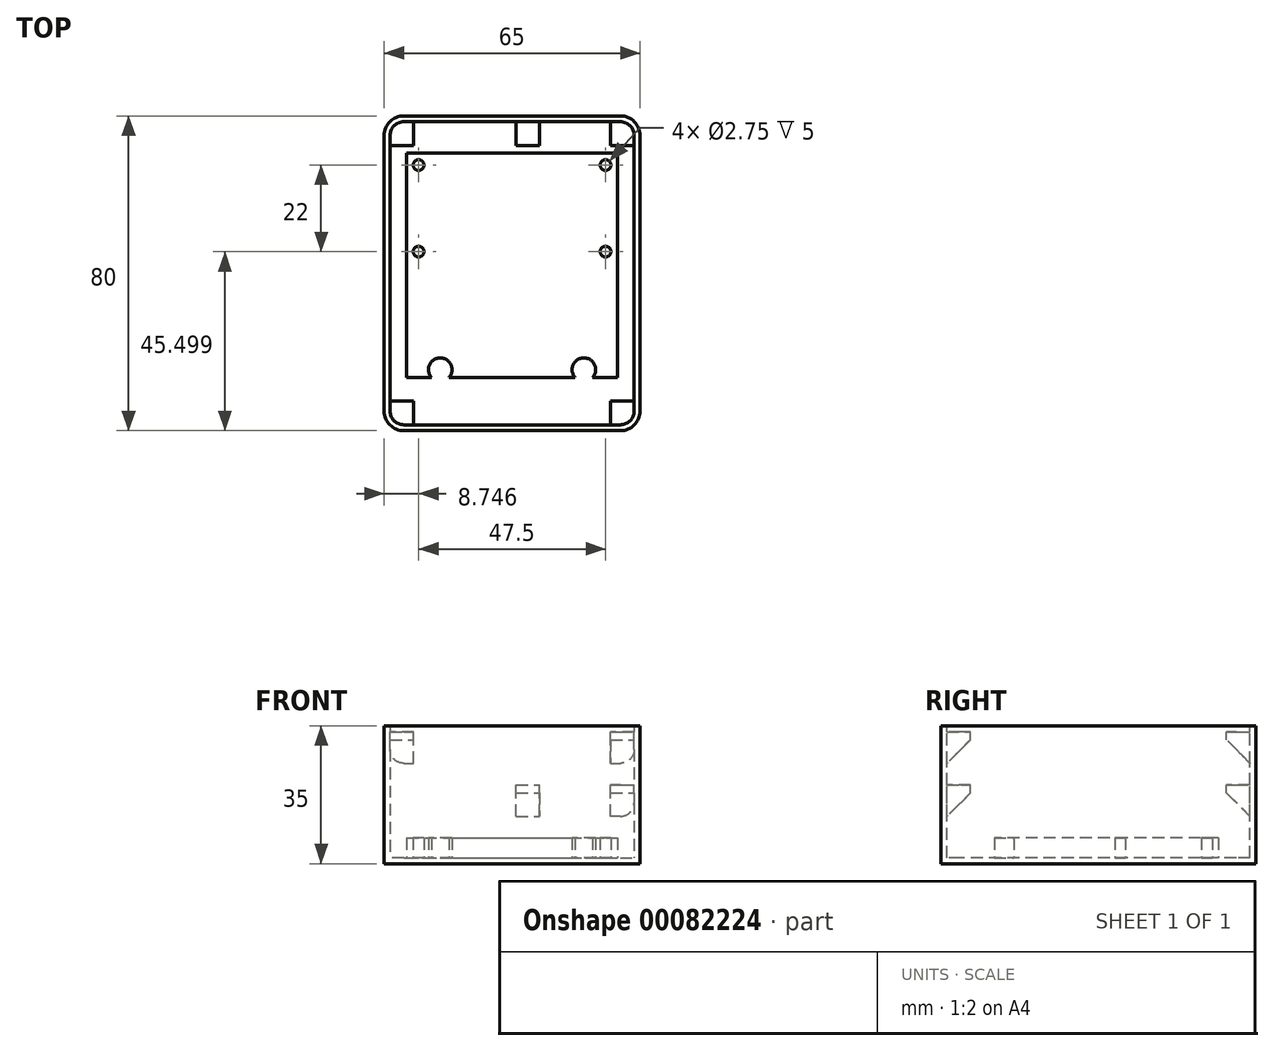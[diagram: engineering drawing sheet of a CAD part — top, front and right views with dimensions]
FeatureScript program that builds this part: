
annotation { "Feature Type Name" : "Feature", "Feature Type Description" : "" }
export const myFeature = defineFeature(function(context is Context, id is Id, definition is map)
    precondition{}
    {
        {
            var Q0;
            Q0=qCreatedBy(makeId("Top.planeOp"),FACE);
            var sketch = newSketch(context, id + "F0", { "sketchPlane" : qUnion([Q0])});
            skLineSegment(sketch, "E0.bottom", {"start": v(-31.3, 26.17) * mm, "end": v(33.7, 26.17) * mm});
            skLineSegment(sketch, "E0.top", {"start": v(-31.3, -53.83) * mm, "end": v(33.7, -53.83) * mm});
            skLineSegment(sketch, "E0.left", {"start": v(-31.3, 26.17) * mm, "end": v(-31.3, -53.83) * mm});
            skLineSegment(sketch, "E0.right", {"start": v(33.7, 26.17) * mm, "end": v(33.7, -53.83) * mm});
            skSolve(sketch);
        }
        {
            var Q0;
            Q0 = qSketchRegion(id + "F0", true);
            extrude(context, id + "F1", {"entities" : qUnion([Q0]), "depth" : 35 * mm});
        }
        {
            var Q0;
            Q0=makeQuery(id+"F1.opExtrude","SWEPT_EDGE",EDGE,{"disambiguationData":[OSD([sQuery(id+"F0.wireOp",EDGE,"E0.top"),sQuery(id+"F0.wireOp",EDGE,"E0.left")])]});
            var Q1;
            Q1=makeQuery(id+"F1.opExtrude","SWEPT_EDGE",EDGE,{"disambiguationData":[OSD([sQuery(id+"F0.wireOp",EDGE,"E0.bottom"),sQuery(id+"F0.wireOp",EDGE,"E0.left")])]});
            var Q2;
            Q2=makeQuery(id+"F1.opExtrude","SWEPT_EDGE",EDGE,{"disambiguationData":[OSD([sQuery(id+"F0.wireOp",EDGE,"E0.top"),sQuery(id+"F0.wireOp",EDGE,"E0.right")])]});
            var Q3;
            Q3=makeQuery(id+"F1.opExtrude","SWEPT_EDGE",EDGE,{"disambiguationData":[OSD([sQuery(id+"F0.wireOp",EDGE,"E0.bottom"),sQuery(id+"F0.wireOp",EDGE,"E0.right")])]});
            fillet(context, id + "F2", {"entities" : qUnion([Q0, Q1, Q2, Q3]), "radius" : 5 * mm, "tangentPropagation" : true, "allowEdgeOverflow" : false});
        }
        {
            var Q0;
            Q0=makeQuery(id+"F1.opExtrude","CAP_FACE",FACE,{"disambiguationData":[OSD([sQuery(id+"F0.wireOp",EDGE,"E0.bottom"),sQuery(id+"F0.wireOp",EDGE,"E0.top"),sQuery(id+"F0.wireOp",EDGE,"E0.left"),sQuery(id+"F0.wireOp",EDGE,"E0.right")])],"isStart":false});
            shell(context, id + "F3", {"entities" : qUnion([Q0]), "thickness" : 1.5 * mm});
        }
        {
            var Q0;
            Q0=makeQuery(id+"F3.opShell","OFFSET_FACE",FACE,{"disambiguationData":[OSD([sQuery(id+"F0.wireOp",EDGE,"E0.bottom"),sQuery(id+"F0.wireOp",EDGE,"E0.top"),sQuery(id+"F0.wireOp",EDGE,"E0.left"),sQuery(id+"F0.wireOp",EDGE,"E0.right")])]});
            cPlane(context, id + "F4", {"entities" : qUnion([Q0]), "cplaneType" : CPlaneType.OFFSET, "offset" : 32 * mm, "width" : 150 * mm, "height" : 150 * mm});
        }
        {
            var Q0;
            Q0=qCreatedBy(id+"F4.planeOp",FACE);
            var sketch = newSketch(context, id + "F5", { "sketchPlane" : qUnion([Q0])});
            skLineSegment(sketch, "E1.bottom", {"start": v(-23.8, 18.67) * mm, "end": v(-31.3, 18.67) * mm});
            skLineSegment(sketch, "E1.top", {"start": v(-23.8, 26.17) * mm, "end": v(-31.3, 26.17) * mm});
            skLineSegment(sketch, "E1.left", {"start": v(-23.8, 18.67) * mm, "end": v(-23.8, 26.17) * mm});
            skLineSegment(sketch, "E1.right", {"start": v(-31.3, 18.67) * mm, "end": v(-31.3, 26.17) * mm});
            skLineSegment(sketch, "E2.bottom", {"start": v(33.7, 26.17) * mm, "end": v(26.2, 26.17) * mm});
            skLineSegment(sketch, "E2.top", {"start": v(33.7, 18.67) * mm, "end": v(26.2, 18.67) * mm});
            skLineSegment(sketch, "E2.left", {"start": v(33.7, 26.17) * mm, "end": v(33.7, 18.67) * mm});
            skLineSegment(sketch, "E2.right", {"start": v(26.2, 26.17) * mm, "end": v(26.2, 18.67) * mm});
            skLineSegment(sketch, "E3.bottom", {"start": v(33.7, -53.83) * mm, "end": v(26.2, -53.83) * mm});
            skLineSegment(sketch, "E3.top", {"start": v(33.7, -46.33) * mm, "end": v(26.2, -46.33) * mm});
            skLineSegment(sketch, "E3.left", {"start": v(33.7, -53.83) * mm, "end": v(33.7, -46.33) * mm});
            skLineSegment(sketch, "E3.right", {"start": v(26.2, -53.83) * mm, "end": v(26.2, -46.33) * mm});
            skLineSegment(sketch, "E4.bottom", {"start": v(-31.3, -53.83) * mm, "end": v(-23.8, -53.83) * mm});
            skLineSegment(sketch, "E4.top", {"start": v(-31.3, -46.33) * mm, "end": v(-23.8, -46.33) * mm});
            skLineSegment(sketch, "E4.left", {"start": v(-31.3, -53.83) * mm, "end": v(-31.3, -46.33) * mm});
            skLineSegment(sketch, "E4.right", {"start": v(-23.8, -53.83) * mm, "end": v(-23.8, -46.33) * mm});
            skLineSegment(sketch, "E5.0", {"start": v(-29.8, 21.17) * mm, "end": v(-29.8, -48.83) * mm});
            skArc(sketch, "E6.0", {"start": v(-26.3, 24.67) * mm, "mid": v(-28.77, 23.64) * mm, "end": v(-29.8, 21.17) * mm});
            skLineSegment(sketch, "E7.0", {"start": v(-26.3, 24.67) * mm, "end": v(28.7, 24.67) * mm});
            skArc(sketch, "E8.0", {"start": v(32.2, 21.17) * mm, "mid": v(31.18, 23.64) * mm, "end": v(28.7, 24.67) * mm});
            skLineSegment(sketch, "E9.0", {"start": v(32.2, 21.17) * mm, "end": v(32.2, -48.83) * mm});
            skPoint(sketch, "E10.0", {"position": v(31.18, -51.3) * mm});
            skLineSegment(sketch, "E11.0", {"start": v(-26.3, -52.33) * mm, "end": v(28.7, -52.33) * mm});
            skArc(sketch, "E12.0", {"start": v(28.7, -52.33) * mm, "mid": v(31.18, -51.3) * mm, "end": v(32.2, -48.83) * mm});
            skArc(sketch, "E13.0", {"start": v(-29.8, -48.83) * mm, "mid": v(-28.77, -51.3) * mm, "end": v(-26.3, -52.33) * mm});
            skSolve(sketch);
        }
        {
            var Q0;
            {var subQ0=sQuery(id+"F5.wireOp",EDGE,"E6.0");Q0=makeQuery(id+"F5.imprint","IMPRINT",FACE,{"disambiguationData":[TD([[makeQuery(id+"F5.imprint","IMPRINT",EDGE,{"derivedFrom":subQ0}),1.0]])]});}
            var Q1;
            {var subQ0=sQuery(id+"F5.wireOp",EDGE,"E8.0");Q1=makeQuery(id+"F5.imprint","IMPRINT",FACE,{"disambiguationData":[TD([[makeQuery(id+"F5.imprint","IMPRINT",EDGE,{"derivedFrom":subQ0}),1.0]])]});}
            var Q2;
            {var subQ0=sQuery(id+"F5.wireOp",EDGE,"E12.0");Q2=makeQuery(id+"F5.imprint","IMPRINT",FACE,{"disambiguationData":[TD([[makeQuery(id+"F5.imprint","IMPRINT",EDGE,{"derivedFrom":subQ0}),1.0]])]});}
            var Q3;
            {var subQ0=sQuery(id+"F5.wireOp",EDGE,"E13.0");Q3=makeQuery(id+"F5.imprint","IMPRINT",FACE,{"disambiguationData":[TD([[makeQuery(id+"F5.imprint","IMPRINT",EDGE,{"derivedFrom":subQ0}),1.0]])]});}
            extrude(context, id + "F6", {"entities" : qUnion([Q0, Q1, Q2, Q3]), "operationType" : NewBodyOperationType.ADD, "oppositeDirection" : true, "depth" : 8 * mm});
        }
        {
            var Q0;
            Q0=makeQuery(id+"F3.opShell","OFFSET_FACE",FACE,{"disambiguationData":[OSD([sQuery(id+"F0.wireOp",EDGE,"E0.bottom"),sQuery(id+"F0.wireOp",EDGE,"E0.top"),sQuery(id+"F0.wireOp",EDGE,"E0.left"),sQuery(id+"F0.wireOp",EDGE,"E0.right")])]});
            var sketch = newSketch(context, id + "F7", { "sketchPlane" : qUnion([Q0])});
            skLineSegment(sketch, "E14.bottom", {"start": v(-25.54, 16.67) * mm, "end": v(27.96, 16.67) * mm});
            skLineSegment(sketch, "E14.top", {"start": v(-25.54, -40.33) * mm, "end": v(27.96, -40.33) * mm});
            skLineSegment(sketch, "E14.left", {"start": v(-25.54, 16.67) * mm, "end": v(-25.54, -40.33) * mm});
            skLineSegment(sketch, "E14.right", {"start": v(27.96, 16.67) * mm, "end": v(27.96, -40.33) * mm});
            skCircle(sketch, "E15", {"center": v(-22.54, 13.67) * mm, "radius": 1.38 * mm});
            skCircle(sketch, "E16", {"center": v(24.96, 13.67) * mm, "radius": 1.38 * mm});
            skCircle(sketch, "E17", {"center": v(-22.54, -8.33) * mm, "radius": 1.38 * mm});
            skCircle(sketch, "E18", {"center": v(24.96, -8.33) * mm, "radius": 1.38 * mm});
            skCircle(sketch, "E19", {"center": v(-22.54, -8.33) * mm, "radius": 2.5 * mm});
            skCircle(sketch, "E20", {"center": v(-22.54, 13.67) * mm, "radius": 2.5 * mm});
            skCircle(sketch, "E21", {"center": v(24.96, 13.67) * mm, "radius": 2.5 * mm});
            skCircle(sketch, "E22", {"center": v(24.96, -8.33) * mm, "radius": 2.5 * mm});
            skCircle(sketch, "E23", {"center": v(19.46, -38.33) * mm, "radius": 3 * mm});
            skCircle(sketch, "E24", {"center": v(-17.04, -38.33) * mm, "radius": 3 * mm});
            skSolve(sketch);
        }
        {
            var Q0;
            Q0=makeQuery(id+"F1.opExtrude","CAP_FACE",FACE,{"disambiguationData":[OSD([sQuery(id+"F0.wireOp",EDGE,"E0.bottom"),sQuery(id+"F0.wireOp",EDGE,"E0.top"),sQuery(id+"F0.wireOp",EDGE,"E0.left"),sQuery(id+"F0.wireOp",EDGE,"E0.right")])],"isStart":false});
            cPlane(context, id + "F8", {"entities" : qUnion([Q0]), "cplaneType" : CPlaneType.OFFSET, "offset" : 15 * mm, "oppositeDirection" : true, "width" : 150 * mm, "height" : 150 * mm});
        }
        {
            var Q0;
            Q0=makeQuery(id+"F7.imprint","IMPRINT",FACE,{"disambiguationData":[TD([[makeQuery(id+"F7.imprint","IMPRINT",EDGE,{"derivedFrom":sQuery(id+"F7.wireOp",EDGE,"E15")}),-1.0]])]});
            var Q1;
            Q1=makeQuery(id+"F7.imprint","IMPRINT",FACE,{"disambiguationData":[TD([[makeQuery(id+"F7.imprint","IMPRINT",EDGE,{"derivedFrom":sQuery(id+"F7.wireOp",EDGE,"E17")}),-1.0]])]});
            var Q2;
            Q2=makeQuery(id+"F7.imprint","IMPRINT",FACE,{"disambiguationData":[TD([[makeQuery(id+"F7.imprint","IMPRINT",EDGE,{"derivedFrom":sQuery(id+"F7.wireOp",EDGE,"E16")}),-1.0]])]});
            var Q3;
            Q3=makeQuery(id+"F7.imprint","IMPRINT",FACE,{"disambiguationData":[TD([[makeQuery(id+"F7.imprint","IMPRINT",EDGE,{"derivedFrom":sQuery(id+"F7.wireOp",EDGE,"E18")}),-1.0]])]});
            var Q4;
            {var subQ0=sQuery(id+"F7.wireOp",EDGE,"E23");var subQ1=sQuery(id+"F7.wireOp",EDGE,"E14.top");var subQ2=makeQuery(id+"F7.imprint","INTERSECT",VERTEX,{"disambiguationData":[OD(0.0)],"derivedFrom":[subQ1,subQ0]});Q4=makeQuery(id+"F7.imprint","IMPRINT",FACE,{"disambiguationData":[TD([[makeQuery(id+"F7.imprint","IMPRINT",EDGE,{"disambiguationData":[TD([[subQ2,-1.0]])],"derivedFrom":subQ1}),1.0]])]});}
            var Q5;
            {var subQ0=sQuery(id+"F7.wireOp",EDGE,"E24");var subQ1=sQuery(id+"F7.wireOp",EDGE,"E14.top");var subQ2=makeQuery(id+"F7.imprint","INTERSECT",VERTEX,{"disambiguationData":[OD(0.0)],"derivedFrom":[subQ1,subQ0]});Q5=makeQuery(id+"F7.imprint","IMPRINT",FACE,{"disambiguationData":[TD([[makeQuery(id+"F7.imprint","IMPRINT",EDGE,{"disambiguationData":[TD([[subQ2,-1.0]])],"derivedFrom":subQ1}),1.0]])]});}
            extrude(context, id + "F9", {"entities" : qUnion([Q0, Q1, Q2, Q3, Q4, Q5]), "operationType" : NewBodyOperationType.ADD, "depth" : 5 * mm});
        }
        {
            var Q0;
            Q0=qCreatedBy(id+"F8.planeOp",FACE);
            var sketch = newSketch(context, id + "F10", { "sketchPlane" : qUnion([Q0])});
            skLineSegment(sketch, "E25.bottom", {"start": v(2.2, 26.17) * mm, "end": v(8.2, 26.17) * mm});
            skLineSegment(sketch, "E25.top", {"start": v(2.2, 18.67) * mm, "end": v(8.2, 18.67) * mm});
            skLineSegment(sketch, "E25.left", {"start": v(2.2, 26.17) * mm, "end": v(2.2, 18.67) * mm});
            skLineSegment(sketch, "E25.right", {"start": v(8.2, 26.17) * mm, "end": v(8.2, 18.67) * mm});
            skLineSegment(sketch, "E26.0.0", {"start": v(-31.3, 21.17) * mm, "end": v(-31.3, -48.83) * mm});
            skArc(sketch, "E26.0.1", {"start": v(-31.3, -48.83) * mm, "mid": v(-29.83, -52.37) * mm, "end": v(-26.3, -53.83) * mm});
            skLineSegment(sketch, "E26.0.2", {"start": v(-26.3, -53.83) * mm, "end": v(28.7, -53.83) * mm});
            skArc(sketch, "E26.0.3", {"start": v(28.7, -53.83) * mm, "mid": v(32.24, -52.37) * mm, "end": v(33.7, -48.83) * mm});
            skLineSegment(sketch, "E26.0.4", {"start": v(33.7, -48.83) * mm, "end": v(33.7, 21.17) * mm});
            skArc(sketch, "E26.0.5", {"start": v(33.7, 21.17) * mm, "mid": v(32.24, 24.7) * mm, "end": v(28.7, 26.17) * mm});
            skLineSegment(sketch, "E26.0.6", {"start": v(28.7, 26.17) * mm, "end": v(-26.3, 26.17) * mm});
            skArc(sketch, "E26.0.7", {"start": v(-26.3, 26.17) * mm, "mid": v(-29.83, 24.7) * mm, "end": v(-31.3, 21.17) * mm});
            skLineSegment(sketch, "E27.0.0", {"start": v(32.2, 18.67) * mm, "end": v(32.2, 21.17) * mm});
            skArc(sketch, "E27.0.1", {"start": v(32.2, 21.17) * mm, "mid": v(31.18, 23.64) * mm, "end": v(28.7, 24.67) * mm});
            skLineSegment(sketch, "E27.0.2", {"start": v(28.7, 24.67) * mm, "end": v(26.2, 24.67) * mm});
            skLineSegment(sketch, "E27.0.3", {"start": v(26.2, 24.67) * mm, "end": v(26.2, 18.67) * mm});
            skLineSegment(sketch, "E27.0.4", {"start": v(26.2, 18.67) * mm, "end": v(32.2, 18.67) * mm});
            skLineSegment(sketch, "E28.0.0", {"start": v(26.2, -46.33) * mm, "end": v(26.2, -52.33) * mm});
            skLineSegment(sketch, "E28.0.1", {"start": v(26.2, -52.33) * mm, "end": v(28.7, -52.33) * mm});
            skArc(sketch, "E28.0.2", {"start": v(28.7, -52.33) * mm, "mid": v(31.18, -51.3) * mm, "end": v(32.2, -48.83) * mm});
            skLineSegment(sketch, "E28.0.3", {"start": v(32.2, -48.83) * mm, "end": v(32.2, -46.33) * mm});
            skLineSegment(sketch, "E28.0.4", {"start": v(32.2, -46.33) * mm, "end": v(26.2, -46.33) * mm});
            skLineSegment(sketch, "E29.MirrorCS", {"start": v(2.2, -53.83) * mm, "end": v(8.2, -53.83) * mm});
            skLineSegment(sketch, "E30.MirrorCS", {"start": v(8.2, -53.83) * mm, "end": v(8.2, -46.33) * mm});
            skLineSegment(sketch, "E31.MirrorCS", {"start": v(2.2, -53.83) * mm, "end": v(2.2, -46.33) * mm});
            skLineSegment(sketch, "E32.MirrorCS", {"start": v(2.2, -46.33) * mm, "end": v(8.2, -46.33) * mm});
            skSolve(sketch);
        }
        {
            var Q0;
            Q0=makeQuery(id+"F10.imprint","IMPRINT",FACE,{"disambiguationData":[TD([[makeQuery(id+"F10.imprint","IMPRINT",EDGE,{"derivedFrom":sQuery(id+"F10.wireOp",EDGE,"E25.top")}),1.0]])]});
            var Q1;
            Q1=makeQuery(id+"F10.imprint","IMPRINT",FACE,{"disambiguationData":[TD([[makeQuery(id+"F10.imprint","IMPRINT",EDGE,{"derivedFrom":sQuery(id+"F10.wireOp",EDGE,"E27.0.0")}),1.0]])]});
            var Q2;
            Q2=makeQuery(id+"F10.imprint","IMPRINT",FACE,{"disambiguationData":[TD([[makeQuery(id+"F10.imprint","IMPRINT",EDGE,{"derivedFrom":sQuery(id+"F10.wireOp",EDGE,"E28.0.0")}),1.0]])]});
            var Q3;
            Q3=makeQuery(id+"F10.imprint","IMPRINT",FACE,{"disambiguationData":[TD([[makeQuery(id+"F10.imprint","IMPRINT",EDGE,{"derivedFrom":sQuery(id+"F10.wireOp",EDGE,"E29.MirrorCS")}),1.0]])]});
            extrude(context, id + "F11", {"entities" : qUnion([Q0, Q1, Q2, Q3]), "operationType" : NewBodyOperationType.ADD, "oppositeDirection" : true, "depth" : 8 * mm});
        }
        {
            var Q0;
            Q0=makeQuery(id+"F6.opExtrude","CAP_EDGE",EDGE,{"disambiguationData":[OSD([sQuery(id+"F5.wireOp",EDGE,"E3.top")])],"isStart":false});
            var Q1;
            Q1=makeQuery(id+"F11.opExtrude","CAP_EDGE",EDGE,{"disambiguationData":[OSD([sQuery(id+"F10.wireOp",EDGE,"E28.0.4")])],"isStart":false});
            var Q2;
            Q2=makeQuery(id+"F11.opExtrude","CAP_EDGE",EDGE,{"disambiguationData":[OSD([sQuery(id+"F10.wireOp",EDGE,"E32.MirrorCS")])],"isStart":false});
            var Q3;
            Q3=makeQuery(id+"F11.opExtrude","CAP_EDGE",EDGE,{"disambiguationData":[OSD([sQuery(id+"F10.wireOp",EDGE,"E27.0.4")])],"isStart":false});
            var Q4;
            Q4=makeQuery(id+"F6.opExtrude","CAP_EDGE",EDGE,{"disambiguationData":[OSD([sQuery(id+"F5.wireOp",EDGE,"E2.top")])],"isStart":false});
            var Q5;
            Q5=makeQuery(id+"F11.opExtrude","CAP_EDGE",EDGE,{"disambiguationData":[OSD([sQuery(id+"F10.wireOp",EDGE,"E25.top")])],"isStart":false});
            var Q6;
            Q6=makeQuery(id+"F6.opExtrude","CAP_EDGE",EDGE,{"disambiguationData":[OSD([sQuery(id+"F5.wireOp",EDGE,"E1.bottom")])],"isStart":false});
            var Q7;
            Q7=makeQuery(id+"F6.opExtrude","CAP_EDGE",EDGE,{"disambiguationData":[OSD([sQuery(id+"F5.wireOp",EDGE,"E4.top")])],"isStart":false});
            chamfer(context, id + "F12", {"entities" : qUnion([Q0, Q1, Q2, Q3, Q4, Q5, Q6, Q7]), "width" : 6 * mm, "tangentPropagation" : true});
        }
    });
